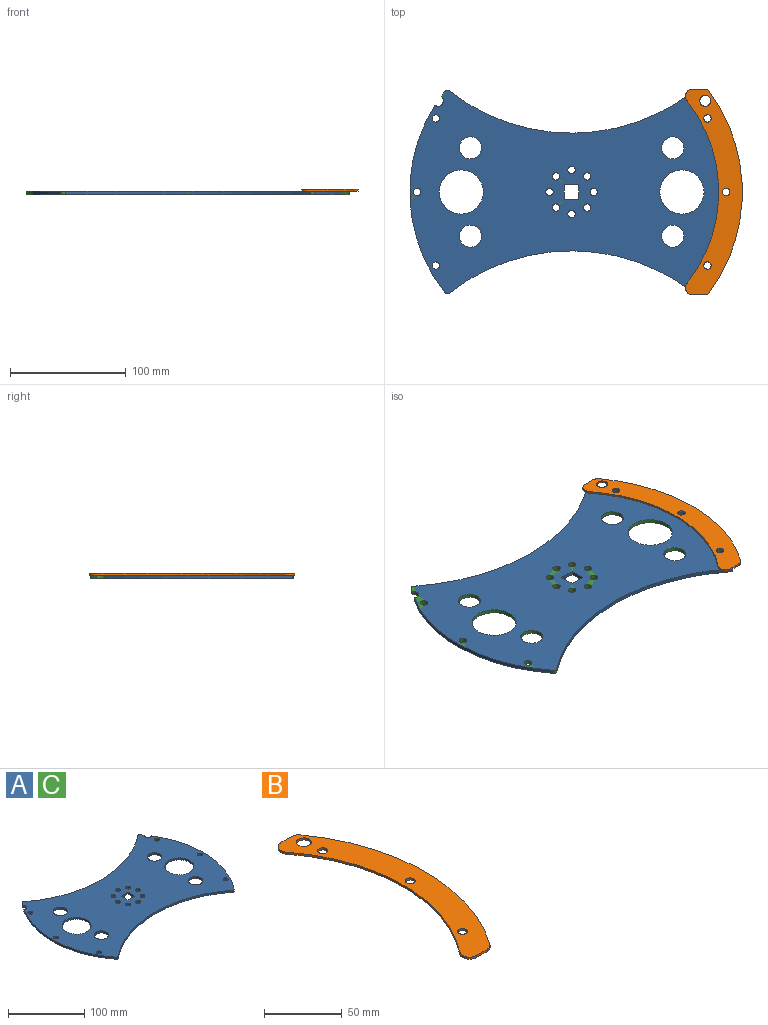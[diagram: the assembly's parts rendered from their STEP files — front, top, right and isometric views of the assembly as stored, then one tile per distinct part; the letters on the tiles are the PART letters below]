
ASSEMBLY  parts=3 mates=1
PART A: 38 faces, bbox 279.4x175.8x3.2 mm
  f0: plane 12.75x3.18mm, normal (0,-1,0), area 40.5mm2, adj f1,f35,f36,f37
  f1: plane 12.75x3.18mm, normal (-1,0,0), area 40.5mm2, adj f0,f2,f36,f37
  f2: plane 12.75x3.18mm, normal (0,1,0), area 40.5mm2, adj f1,f35,f36,f37
  f3: cylinder r=2.54mm len=3.55mm, axis (0,0,-1), area 12.6mm2, adj f4,f14,f36,f37
  f4: cylinder r=139.7mm len=161.7mm, axis (0,0,-1), area 548.4mm2, adj f3,f5,f36,f37
  f5: cylinder r=4.76mm len=8.65mm, axis (0,0,-1), area 47mm2, adj f4,f6,f36,f37
  f6: cylinder r=139.7mm len=4.29mm, axis (0,0,-1), area 17.2mm2, adj f5,f7,f36,f37
  f7: cylinder r=2.54mm len=3.55mm, axis (0,0,-1), area 12.6mm2, adj f6,f8,f36,f37
  f8: extruded ~211.61x36.55mm, area 724.1mm2, adj f7,f9,f36,f37
  f9: cylinder r=2.54mm len=3.55mm, axis (0,0,-1), area 12.6mm2, adj f8,f10,f36,f37
  f10: cylinder r=139.7mm len=4.29mm, axis (0,0,-1), area 17.2mm2, adj f9,f11,f36,f37
  f11: cylinder r=4.76mm len=8.65mm, axis (0,0,-1), area 47mm2, adj f10,f12,f36,f37
  f12: cylinder r=139.7mm len=161.7mm, axis (0,0,-1), area 548.4mm2, adj f11,f13,f36,f37
  f13: cylinder r=2.54mm len=3.55mm, axis (0,0,-1), area 12.6mm2, adj f12,f14,f36,f37
  f14: extruded ~211.61x36.55mm, area 724.1mm2, adj f3,f13,f36,f37
  f15: cylinder r=19.05mm len=38.1mm, axis (0,0,-1), area 380mm2, adj f36,f37
  f16: cylinder r=9.53mm len=19.05mm, axis (0,0,-1), area 190mm2, adj f36,f37
  f17: cylinder r=9.53mm len=19.05mm, axis (0,0,-1), area 190mm2, adj f36,f37
  f18: cylinder r=3.17mm len=6.35mm, axis (0,0,-1), area 63.3mm2, adj f36,f37
  f19: cylinder r=3.17mm len=6.35mm, axis (0,0,-1), area 63.3mm2, adj f36,f37
  f20: cylinder r=3.17mm len=6.35mm, axis (0,0,-1), area 63.3mm2, adj f36,f37
  f21: cylinder r=3.17mm len=6.35mm, axis (0,0,-1), area 63.3mm2, adj f36,f37
  f22: cylinder r=3.17mm len=6.35mm, axis (0,0,-1), area 63.3mm2, adj f36,f37
  f23: cylinder r=3.17mm len=6.35mm, axis (0,0,-1), area 63.3mm2, adj f36,f37
  f24: cylinder r=3.17mm len=6.35mm, axis (0,0,-1), area 63.3mm2, adj f36,f37
  f25: cylinder r=3.17mm len=6.35mm, axis (0,0,-1), area 63.3mm2, adj f36,f37
  f26: cylinder r=3.17mm len=6.35mm, axis (0,0,-1), area 63.3mm2, adj f36,f37
  f27: cylinder r=3.17mm len=6.35mm, axis (0,0,-1), area 63.3mm2, adj f36,f37
  f28: cylinder r=3.17mm len=6.35mm, axis (0,0,-1), area 63.3mm2, adj f36,f37
  f29: cylinder r=3.17mm len=6.35mm, axis (0,0,-1), area 63.3mm2, adj f36,f37
  f30: cylinder r=3.17mm len=6.35mm, axis (0,0,-1), area 63.3mm2, adj f36,f37
  f31: cylinder r=3.17mm len=6.35mm, axis (0,0,-1), area 63.3mm2, adj f36,f37
  f32: cylinder r=9.53mm len=19.05mm, axis (0,0,-1), area 190mm2, adj f36,f37
  f33: cylinder r=19.05mm len=38.1mm, axis (0,0,-1), area 380mm2, adj f36,f37
  f34: cylinder r=9.53mm len=19.05mm, axis (0,0,-1), area 190mm2, adj f36,f37
  f35: plane 12.75x3.18mm, normal (1,0,0), area 40.5mm2, adj f0,f2,f36,f37
  f36: plane 279.4x175.78mm, normal (0,0,1), area 30766.9mm2, adj f0,f1,f2,f3,f4,f5,f6,f7
  f37: plane 279.4x175.78mm, normal (0,0,-1), area 30766.9mm2, adj f0,f1,f2,f3,f4,f5,f6,f7
PART B: 14 faces, bbox 48.9x177.8x1.6 mm
  f0: plane 9.55x1.59mm, normal (0,1,0), area 15.2mm2, adj f1,f11,f12,f13
  f1: cylinder r=6.35mm len=10.28mm, axis (0,0,-1), area 22.6mm2, adj f0,f2,f12,f13
  f2: cylinder r=127mm len=157.25mm, axis (0,0,-1), area 269.2mm2, adj f1,f3,f12,f13
  f3: cylinder r=6.35mm len=10.28mm, axis (0,0,-1), area 22.6mm2, adj f2,f4,f12,f13
  f4: plane 9.55x1.59mm, normal (0,-1,0), area 15.2mm2, adj f3,f5,f12,f13
  f5: cylinder r=6.35mm len=5.15mm, axis (0,0,-1), area 9.5mm2, adj f4,f6,f12,f13
  f6: cylinder r=147.32mm len=172.55mm, axis (0,0,-1), area 292.6mm2, adj f5,f11,f12,f13
  f7: cylinder r=4.76mm len=9.53mm, axis (0,0,-1), area 47.5mm2, adj f12,f13
  f8: cylinder r=3.17mm len=6.35mm, axis (0,0,-1), area 31.7mm2, adj f12,f13
  f9: cylinder r=3.17mm len=6.35mm, axis (0,0,-1), area 31.7mm2, adj f12,f13
  f10: cylinder r=3.17mm len=6.35mm, axis (0,0,-1), area 31.7mm2, adj f12,f13
  f11: cylinder r=6.35mm len=5.15mm, axis (0,0,-1), area 9.5mm2, adj f0,f6,f12,f13
  f12: plane 177.81x48.95mm, normal (0,0,1), area 3682.5mm2, adj f0,f1,f2,f3,f4,f5,f6,f7
  f13: plane 177.81x48.95mm, normal (0,0,-1), area 3682.5mm2, adj f0,f1,f2,f3,f4,f5,f6,f7
PART C: same geometry as A
PLACE A t=(-45.54,47.45,1.7)mm
PLACE B t=(-45.54,47.45,4.87)mm
PLACE C t=(-45.54,47.45,1.7)mm
MATE fastened B.f9 <-> A.f22  axis (0,0,-1) through (87.81,47.45,4.87)mm
